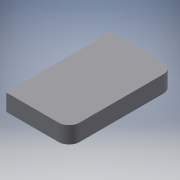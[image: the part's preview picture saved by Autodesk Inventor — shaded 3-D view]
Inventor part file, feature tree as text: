
AUTODESK INVENTOR PART (.ipt)
format: ipt  version: 2018 (Build 220112000, 112)  size: 96,768 bytes
history: native  units: mm
features: extrude x1, fillet x1, sketch x1
ambient origin geometry x8: Origin, YZ Plane, XZ Plane, XY Plane, X Axis, Y Axis, Z Axis, Center Point
bodies: Solido1 (feature_tree)
feature tree (3):
  extrude  "Estrusione1"  Depth=30.0mm
  fillet  "Raccordo1"  Radius=50.0mm
  sketch  "Schizzo1"
